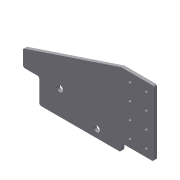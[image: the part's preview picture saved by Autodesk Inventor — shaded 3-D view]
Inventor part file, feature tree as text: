
AUTODESK INVENTOR PART (.ipt)
format: ipt  version: 2012 (Build 160160000, 160)  size: 142,848 bytes
history: native  units: in
note: dims shown in document units (in); Inventor stores cm internally (conversion verified against a paired STEP export)
features: extrude x5, sketch x5, pattern_linear x1, fillet x1
ambient origin geometry x8: Origin, YZ Plane, XZ Plane, XY Plane, X Axis, Y Axis, Z Axis, Center Point
bodies: Solid1 (feature_tree)
feature tree (12):
  extrude  "Extrusion1"  Depth=5.0in
  extrude  "Extrusion2"  Depth=0.1875in
  pattern_linear  "Rectangular Pattern1"  Count1=4 Spacing1=1.0in
  extrude  "Extrusion3"  Depth=0.375in
  extrude  "Extrusion4"  Depth=3.5in
  extrude  "Extrusion5"  Depth=0.5in
  fillet  "Fillet1"  Radius=2.25in
  sketch  "Sketch1"  dims[d0=8.0in d1=5.0in]
  sketch  "Sketch2"  dims[d2=0.1875in d3=0.0in d4=0.1875in]
  sketch  "Sketch3"  dims[d5=1.0in]
  sketch  "Sketch4"  dims[d6=0.5in]
  sketch  "Sketch5"  dims[d7=0.25in d8=0.0in d9=1.5748in d11=1.0in d12=0.7874in d14=1.0in d15=0.375in d16=3.5in d17=0.5in d18=2.25in d19=1.0in d20=0.25in d21=0.0in d22=1.5in d23=1.0in d24=2.0in d25=0.5in d26=0.5in d27=0.25in d28=0.0in d29=1.0in d30=2.0in d31=0.25in d32=0.0in d33=0.125in]
